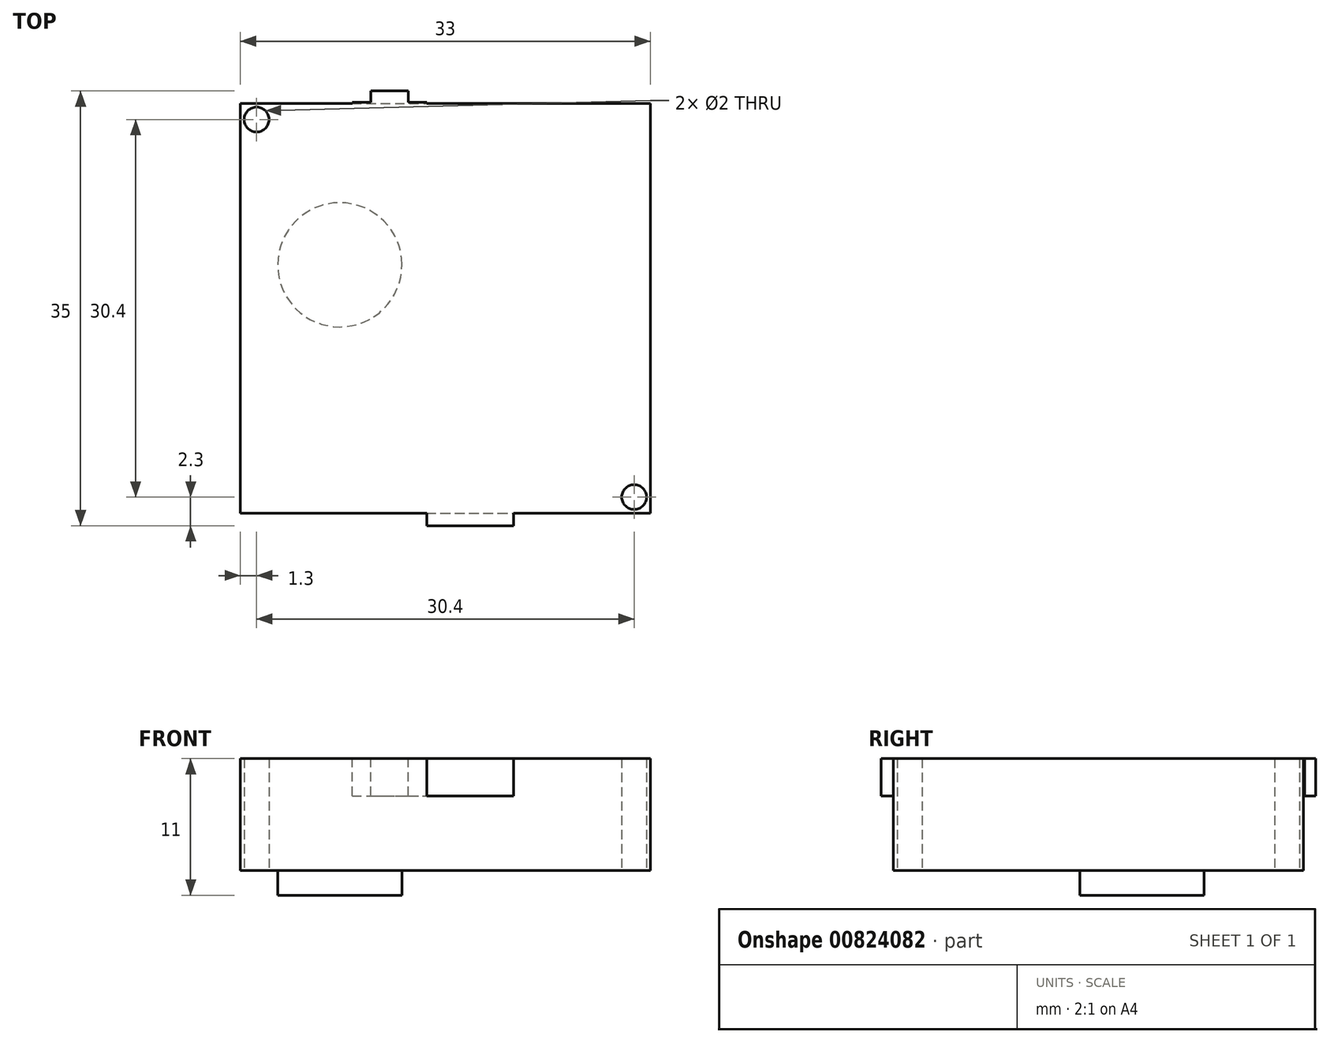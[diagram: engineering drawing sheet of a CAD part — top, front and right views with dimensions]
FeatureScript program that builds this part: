
annotation { "Feature Type Name" : "Feature", "Feature Type Description" : "" }
export const myFeature = defineFeature(function(context is Context, id is Id, definition is map)
    precondition{}
    {
        {
            var Q0;
            Q0=qCreatedBy(makeId("Top.planeOp"),FACE);
            var sketch = newSketch(context, id + "F0", { "sketchPlane" : qUnion([Q0])});
            skLineSegment(sketch, "E0.bottom", {"start": v(-16.5, 16.5) * mm, "end": v(16.5, 16.5) * mm});
            skLineSegment(sketch, "E0.top", {"start": v(-16.5, -16.5) * mm, "end": v(16.5, -16.5) * mm});
            skLineSegment(sketch, "E0.left", {"start": v(-16.5, 16.5) * mm, "end": v(-16.5, -16.5) * mm});
            skLineSegment(sketch, "E0.right", {"start": v(16.5, 16.5) * mm, "end": v(16.5, -16.5) * mm});
            skSolve(sketch);
        }
        {
            var Q0;
            Q0=makeQuery(id+"F0.imprint","IMPRINT",FACE,{"disambiguationData":[TD([[makeQuery(id+"F0.imprint","IMPRINT",EDGE,{"derivedFrom":sQuery(id+"F0.wireOp",EDGE,"E0.bottom")}),-1.0]])]});
            extrude(context, id + "F1", {"entities" : qUnion([Q0]), "depth" : 9 * mm, "offsetDistance" : 25 * mm});
        }
        {
            var Q0;
            Q0=makeQuery(id+"F1.opExtrude","CAP_FACE",FACE,{"disambiguationData":[OSD([sQuery(id+"F0.wireOp",EDGE,"E0.bottom"),sQuery(id+"F0.wireOp",EDGE,"E0.top"),sQuery(id+"F0.wireOp",EDGE,"E0.left"),sQuery(id+"F0.wireOp",EDGE,"E0.right")])],"isStart":false});
            var sketch = newSketch(context, id + "F2", { "sketchPlane" : qUnion([Q0])});
            skLineSegment(sketch, "E1.bottom", {"start": v(-7.5, 16.5) * mm, "end": v(-1.5, 16.5) * mm});
            skLineSegment(sketch, "E1.top", {"start": v(-7.5, 16.6) * mm, "end": v(-1.5, 16.6) * mm});
            skLineSegment(sketch, "E1.left", {"start": v(-7.5, 16.5) * mm, "end": v(-7.5, 16.6) * mm});
            skLineSegment(sketch, "E1.right", {"start": v(-1.5, 16.5) * mm, "end": v(-1.5, 16.6) * mm});
            skLineSegment(sketch, "E2.bottom", {"start": v(-6, 16.6) * mm, "end": v(-3, 16.6) * mm});
            skLineSegment(sketch, "E2.top", {"start": v(-6, 17.5) * mm, "end": v(-3, 17.5) * mm});
            skLineSegment(sketch, "E2.left", {"start": v(-6, 16.6) * mm, "end": v(-6, 17.5) * mm});
            skLineSegment(sketch, "E2.right", {"start": v(-3, 16.6) * mm, "end": v(-3, 17.5) * mm});
            skLineSegment(sketch, "E3.bottom", {"start": v(-1.5, -9.92) * mm, "end": v(5.5, -9.92) * mm});
            skLineSegment(sketch, "E3.top", {"start": v(-1.5, -17.5) * mm, "end": v(5.5, -17.5) * mm});
            skLineSegment(sketch, "E3.left", {"start": v(-1.5, -9.92) * mm, "end": v(-1.5, -17.5) * mm});
            skLineSegment(sketch, "E3.right", {"start": v(5.5, -9.92) * mm, "end": v(5.5, -17.5) * mm});
            skSolve(sketch);
        }
        {
            var Q0;
            Q0 = qSketchRegion(id + "F2", true);
            extrude(context, id + "F3", {"entities" : qUnion([Q0]), "operationType" : NewBodyOperationType.ADD, "oppositeDirection" : true, "depth" : 3 * mm, "offsetDistance" : 25 * mm});
        }
        {
            var Q0;
            Q0=makeQuery(id+"F1.opExtrude","CAP_FACE",FACE,{"disambiguationData":[OSD([sQuery(id+"F0.wireOp",EDGE,"E0.bottom"),sQuery(id+"F0.wireOp",EDGE,"E0.top"),sQuery(id+"F0.wireOp",EDGE,"E0.left"),sQuery(id+"F0.wireOp",EDGE,"E0.right")])],"isStart":true});
            var sketch = newSketch(context, id + "F4", { "sketchPlane" : qUnion([Q0])});
            skCircle(sketch, "E4", {"center": v(-8.5, -3.5) * mm, "radius": 5 * mm});
            skSolve(sketch);
        }
        {
            var Q0;
            Q0=makeQuery(id+"F4.imprint","IMPRINT",FACE,{"disambiguationData":[TD([[makeQuery(id+"F4.imprint","IMPRINT",EDGE,{"derivedFrom":sQuery(id+"F4.wireOp",EDGE,"E4")}),1.0]])]});
            extrude(context, id + "F5", {"entities" : qUnion([Q0]), "operationType" : NewBodyOperationType.ADD, "depth" : 2 * mm, "offsetDistance" : 25 * mm});
        }
        {
            var Q0;
            Q0=makeQuery(id+"F1.opExtrude","CAP_FACE",FACE,{"disambiguationData":[OSD([sQuery(id+"F0.wireOp",EDGE,"E0.bottom"),sQuery(id+"F0.wireOp",EDGE,"E0.top"),sQuery(id+"F0.wireOp",EDGE,"E0.left"),sQuery(id+"F0.wireOp",EDGE,"E0.right")])],"isStart":true});
            var sketch = newSketch(context, id + "F6", { "sketchPlane" : qUnion([Q0])});
            skCircle(sketch, "E5", {"center": v(-15.2, -15.2) * mm, "radius": 1 * mm});
            skCircle(sketch, "E6", {"center": v(15.2, 15.2) * mm, "radius": 1 * mm});
            skSolve(sketch);
        }
        {
            var Q0;
            Q0 = qSketchRegion(id + "F6", true);
            extrude(context, id + "F7", {"entities" : qUnion([Q0]), "operationType" : NewBodyOperationType.REMOVE, "oppositeDirection" : true, "depth" : 25 * mm, "offsetDistance" : 25 * mm});
        }
    });
